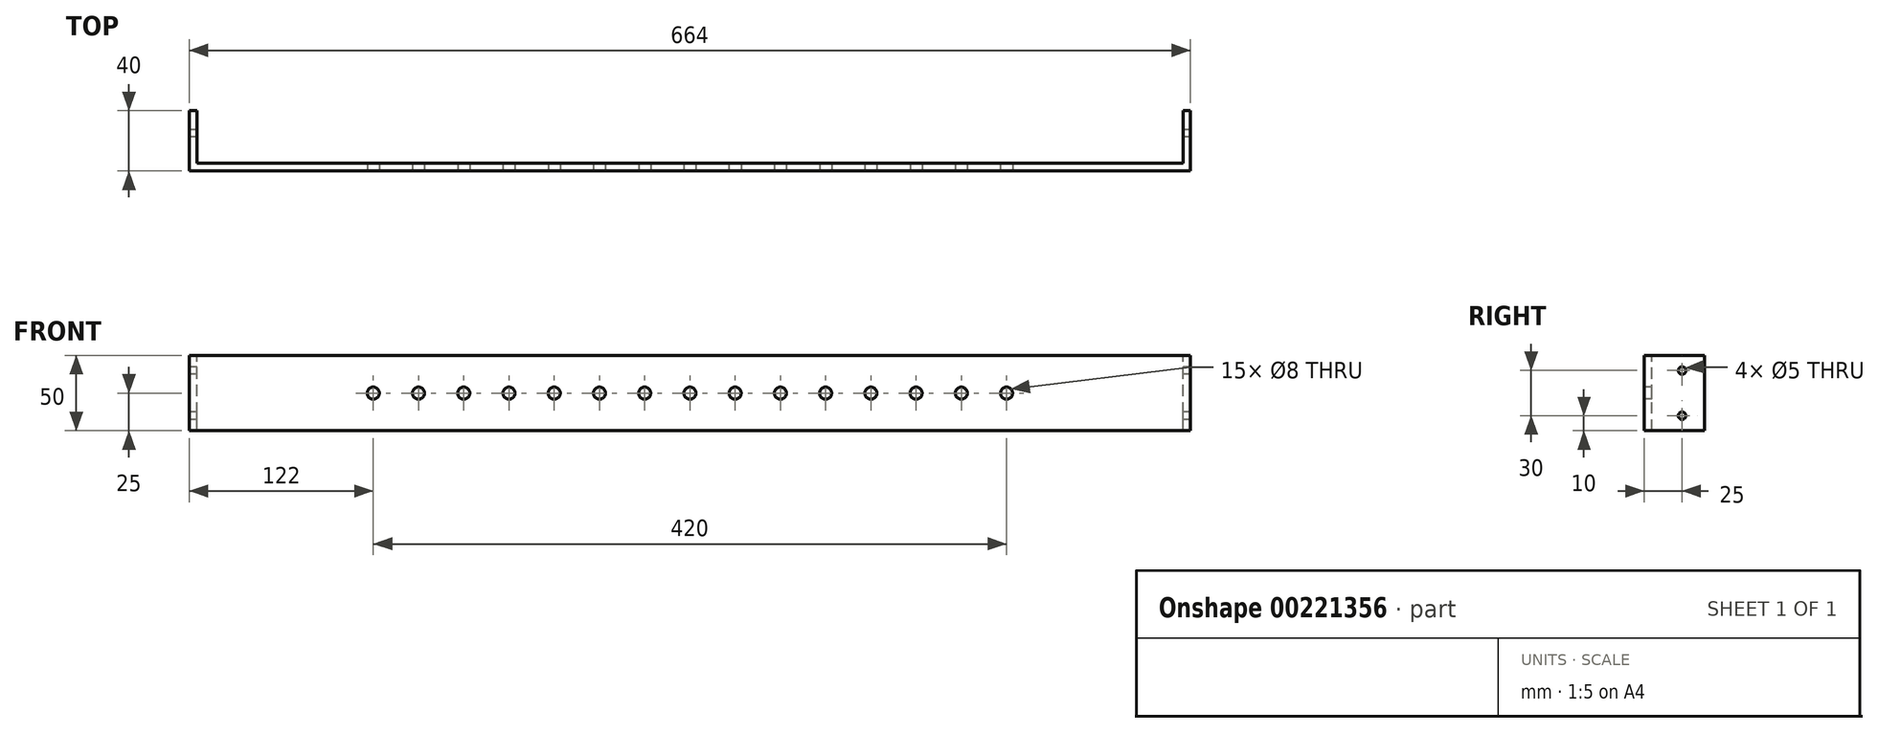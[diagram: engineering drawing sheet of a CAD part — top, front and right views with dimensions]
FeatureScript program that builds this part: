
annotation { "Feature Type Name" : "Feature", "Feature Type Description" : "" }
export const myFeature = defineFeature(function(context is Context, id is Id, definition is map)
    precondition{}
    {
        {
            var Q0;
            Q0=qCreatedBy(makeId("Top.planeOp"),FACE);
            var sketch = newSketch(context, id + "F0", { "sketchPlane" : qUnion([Q0])});
            skLineSegment(sketch, "E0", {"start": v(0, 0) * mm, "end": v(-332, 0) * mm});
            skLineSegment(sketch, "E1", {"start": v(-332, 0) * mm, "end": v(-332, 40) * mm});
            skLineSegment(sketch, "E2.0", {"start": v(-327, 5) * mm, "end": v(-327, 40) * mm});
            skLineSegment(sketch, "E2.1", {"start": v(0, 5) * mm, "end": v(-327, 5) * mm});
            skLineSegment(sketch, "E3", {"start": v(-327, 40) * mm, "end": v(-332, 40) * mm});
            skLineSegment(sketch, "E4", {"start": v(0, 0) * mm, "end": v(0, 5) * mm, "construction": true});
            skLineSegment(sketch, "E5.MirrorCS", {"start": v(0, 0) * mm, "end": v(332, 0) * mm});
            skLineSegment(sketch, "E6.MirrorCS", {"start": v(0, 5) * mm, "end": v(327, 5) * mm});
            skLineSegment(sketch, "E7.MirrorCS", {"start": v(327, 40) * mm, "end": v(332, 40) * mm});
            skLineSegment(sketch, "E8.MirrorCS", {"start": v(327, 5) * mm, "end": v(327, 40) * mm});
            skLineSegment(sketch, "E9.MirrorCS", {"start": v(332, 0) * mm, "end": v(332, 40) * mm});
            skSolve(sketch);
        }
        {
            var Q0;
            Q0 = qSketchRegion(id + "F0", true);
            extrude(context, id + "F1", {"entities" : qUnion([Q0]), "oppositeDirection" : true, "depth" : 50 * mm, "symmetric" : true});
        }
        {
            var Q0;
            Q0=makeQuery(id+"F1.opExtrude","SWEPT_FACE",FACE,{"disambiguationData":[OSD([sQuery(id+"F0.wireOp",EDGE,"E0"),sQuery(id+"F0.wireOp",EDGE,"E5.MirrorCS")])]});
            var sketch = newSketch(context, id + "F2", { "sketchPlane" : qUnion([Q0])});
            skCircle(sketch, "E10", {"center": v(0, 0) * mm, "radius": 4 * mm});
            skCircle(sketch, "E11.1.0.0", {"center": v(30, 0) * mm, "radius": 4 * mm});
            skCircle(sketch, "E11.2.0.0", {"center": v(60, 0) * mm, "radius": 4 * mm});
            skCircle(sketch, "E11.3.0.0", {"center": v(90, 0) * mm, "radius": 4 * mm});
            skCircle(sketch, "E11.4.0.0", {"center": v(120, 0) * mm, "radius": 4 * mm});
            skCircle(sketch, "E11.5.0.0", {"center": v(150, 0) * mm, "radius": 4 * mm});
            skCircle(sketch, "E11.6.0.0", {"center": v(180, 0) * mm, "radius": 4 * mm});
            skCircle(sketch, "E11.7.0.0", {"center": v(210, 0) * mm, "radius": 4 * mm});
            skLineSegment(sketch, "E11.direction1", {"start": v(0, 0) * mm, "end": v(30, 0) * mm, "construction": true});
            skCircle(sketch, "E12.1.0.0", {"center": v(-30, 0) * mm, "radius": 4 * mm});
            skCircle(sketch, "E12.2.0.0", {"center": v(-60, 0) * mm, "radius": 4 * mm});
            skCircle(sketch, "E12.3.0.0", {"center": v(-90, 0) * mm, "radius": 4 * mm});
            skCircle(sketch, "E12.4.0.0", {"center": v(-120, 0) * mm, "radius": 4 * mm});
            skCircle(sketch, "E12.5.0.0", {"center": v(-150, 0) * mm, "radius": 4 * mm});
            skCircle(sketch, "E12.6.0.0", {"center": v(-180, 0) * mm, "radius": 4 * mm});
            skCircle(sketch, "E12.7.0.0", {"center": v(-210, 0) * mm, "radius": 4 * mm});
            skLineSegment(sketch, "E12.direction1", {"start": v(0, 0) * mm, "end": v(-30, 0) * mm, "construction": true});
            skSolve(sketch);
        }
        {
            var Q0;
            Q0 = qSketchRegion(id + "F2", true);
            extrude(context, id + "F3", {"entities" : qUnion([Q0]), "operationType" : NewBodyOperationType.REMOVE, "oppositeDirection" : true, "depth" : 25 * mm});
        }
        {
            var Q0;
            Q0=qCreatedBy(makeId("Right.planeOp"),FACE);
            var sketch = newSketch(context, id + "F4", { "sketchPlane" : qUnion([Q0])});
            skLineSegment(sketch, "E13", {"start": v(0, 0) * mm, "end": v(49.4, 0) * mm, "construction": true});
            skCircle(sketch, "E14", {"center": v(25, 15) * mm, "radius": 2.5 * mm});
            skCircle(sketch, "E15.MirrorC", {"center": v(25, -15) * mm, "radius": 2.5 * mm});
            skSolve(sketch);
        }
        {
            var Q0;
            Q0 = qSketchRegion(id + "F4", true);
            extrude(context, id + "F5", {"entities" : qUnion([Q0]), "operationType" : NewBodyOperationType.REMOVE, "endBound" : BoundingType.THROUGH_ALL, "depth" : 25 * mm, "hasSecondDirection" : true, "secondDirectionBound" : BoundingType.THROUGH_ALL, "secondDirectionOppositeDirection" : true, "secondDirectionDepth" : 25 * mm});
        }
    });
